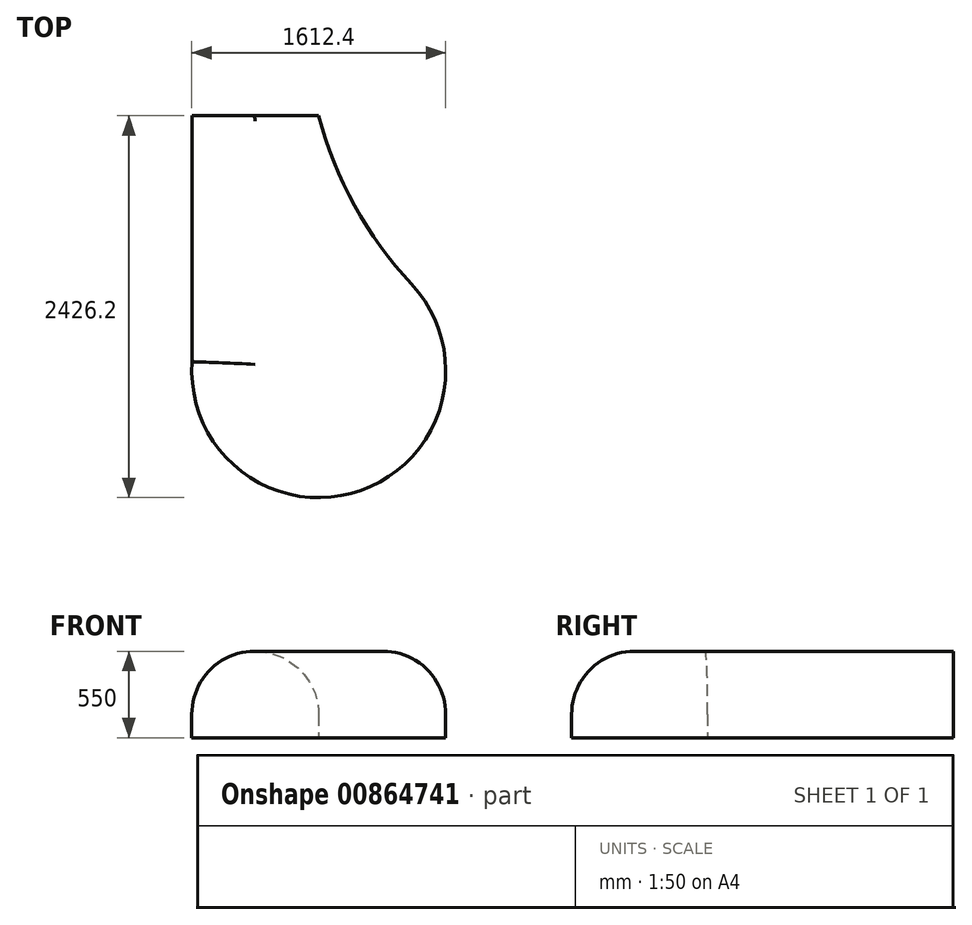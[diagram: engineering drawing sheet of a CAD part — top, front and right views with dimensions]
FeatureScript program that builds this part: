
annotation { "Feature Type Name" : "Feature", "Feature Type Description" : "" }
export const myFeature = defineFeature(function(context is Context, id is Id, definition is map)
    precondition{}
    {
        {
            var Q0;
            Q0=qCreatedBy(makeId("Top.planeOp"),FACE);
            var sketch = newSketch(context, id + "F0", { "sketchPlane" : qUnion([Q0])});
            skLineSegment(sketch, "E0.bottom", {"start": v(0, 0) * mm, "end": v(804.13, 0) * mm});
            skLineSegment(sketch, "E0.top", {"start": v(0, 1620) * mm, "end": v(804.13, 1620) * mm});
            skLineSegment(sketch, "E0.left", {"start": v(0, 0) * mm, "end": v(0, 1620) * mm});
            skLineSegment(sketch, "E0.right", {"start": v(804.13, 0) * mm, "end": v(804.13, 1620) * mm});
            skCircle(sketch, "E1", {"center": v(804.13, 0) * mm, "radius": 806.2 * mm});
            skSolve(sketch);
        }
        {
            var Q0;
            {var subQ0=sQuery(id+"F0.wireOp",EDGE,"E0.top");Q0=makeQuery(id+"F0.imprint","IMPRINT",FACE,{"disambiguationData":[TD([[makeQuery(id+"F0.imprint","IMPRINT",EDGE,{"derivedFrom":subQ0}),-1.0]])]});}
            var Q1;
            {var subQ0=sQuery(id+"F0.wireOp",EDGE,"E0.bottom");Q1=makeQuery(id+"F0.imprint","IMPRINT",FACE,{"disambiguationData":[TD([[makeQuery(id+"F0.imprint","IMPRINT",EDGE,{"derivedFrom":subQ0}),1.0]])]});}
            var Q2;
            {var subQ0=sQuery(id+"F0.wireOp",EDGE,"E0.bottom");Q2=makeQuery(id+"F0.imprint","IMPRINT",FACE,{"disambiguationData":[TD([[makeQuery(id+"F0.imprint","IMPRINT",EDGE,{"derivedFrom":subQ0}),-1.0]])]});}
            extrude(context, id + "F1", {"entities" : qUnion([Q0, Q1, Q2]), "depth" : 550 * mm, "offsetDistance" : 25 * mm});
        }
        {
            var Q0;
            Q0=makeQuery(id+"F1.opExtrude","SWEPT_EDGE",EDGE,{"disambiguationData":[OSD([sQuery(id+"F0.wireOp",EDGE,"E0.right"),sQuery(id+"F0.wireOp",EDGE,"E1")])]});
            fillet(context, id + "F2", {"entities" : qUnion([Q0]), "radius" : 2500 * mm, "tangentPropagation" : true, "allowEdgeOverflow" : false});
        }
        {
            var Q0;
            {var subQ0=sQuery(id+"F0.wireOp",EDGE,"E1");var subQ1=sQuery(id+"F0.wireOp",EDGE,"E0.right");Q0=makeQuery(id+"F2.opFillet","BLEND_EDGE",EDGE,{"blendedFrom":[makeQuery(id+"F1.opExtrude","SWEPT_EDGE",EDGE,{"disambiguationData":[OSD([subQ1,subQ0])]}),makeQuery(id+"F1.opExtrude","CAP_FACE",FACE,{"disambiguationData":[OSD([sQuery(id+"F0.wireOp",EDGE,"E0.top"),sQuery(id+"F0.wireOp",EDGE,"E0.left"),subQ1,subQ0])],"isStart":false})],"blendedInto":[makeQuery(id+"F1.opExtrude","CAP_FACE",FACE,{"disambiguationData":[OSD([sQuery(id+"F0.wireOp",EDGE,"E0.top"),sQuery(id+"F0.wireOp",EDGE,"E0.left"),subQ1,subQ0])],"isStart":false})]});}
            var Q1;
            Q1=makeQuery(id+"F1.opExtrude","CAP_EDGE",EDGE,{"disambiguationData":[OSD([sQuery(id+"F0.wireOp",EDGE,"E0.left")])],"isStart":false});
            var Q2;
            Q2=makeQuery(id+"F1.opExtrude","CAP_EDGE",EDGE,{"disambiguationData":[OSD([sQuery(id+"F0.wireOp",EDGE,"E1")])],"isStart":false});
            fillet(context, id + "F3", {"entities" : qUnion([Q0, Q1, Q2]), "radius" : 400 * mm, "tangentPropagation" : true, "allowEdgeOverflow" : false});
        }
    });
